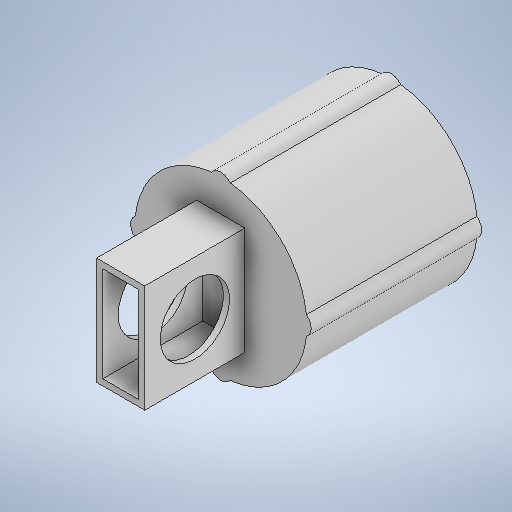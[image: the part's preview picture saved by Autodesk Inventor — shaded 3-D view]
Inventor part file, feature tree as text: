
AUTODESK INVENTOR PART (.ipt)
format: ipt  version: 2025.1 (Build 291241000, 241)  size: 293,376 bytes
history: native  units: mm
features: sketch x4, extrude x3
ambient origin geometry x8: Origin, YZ Plane, XZ Plane, XY Plane, X Axis, Y Axis, Z Axis, Center Point
bodies: Solid1 (feature_tree)
feature tree (7):
  extrude  "Extrusion1"  Depth=10.0mm
  extrude  "Extrusion4"  Depth=70.05mm
  extrude  "Extrusion5"  Depth=74.060786mm
  sketch  "Sketch1"  dims[d0=10.0mm d1=0.25mm]
  sketch  "Skizze - Runde Anordnung1"  dims[d2=40.0mm d4=360.0deg d6=70.05mm]
  sketch  "Skizze4"  dims[d7=0.25mm d8=74.060786mm]
  sketch  "Skizze5"  dims[d9=73.5mm d10=68.9mm d11=0.0mm d24=19.5mm d25=43.5mm d26=2.5mm d27=2.5mm d28=15.5mm d29=2.5mm d30=15.5mm d31=2.5mm d32=40.5mm d33=0.0mm d35=28.0mm d36=0.0mm d37=0.0mm]
